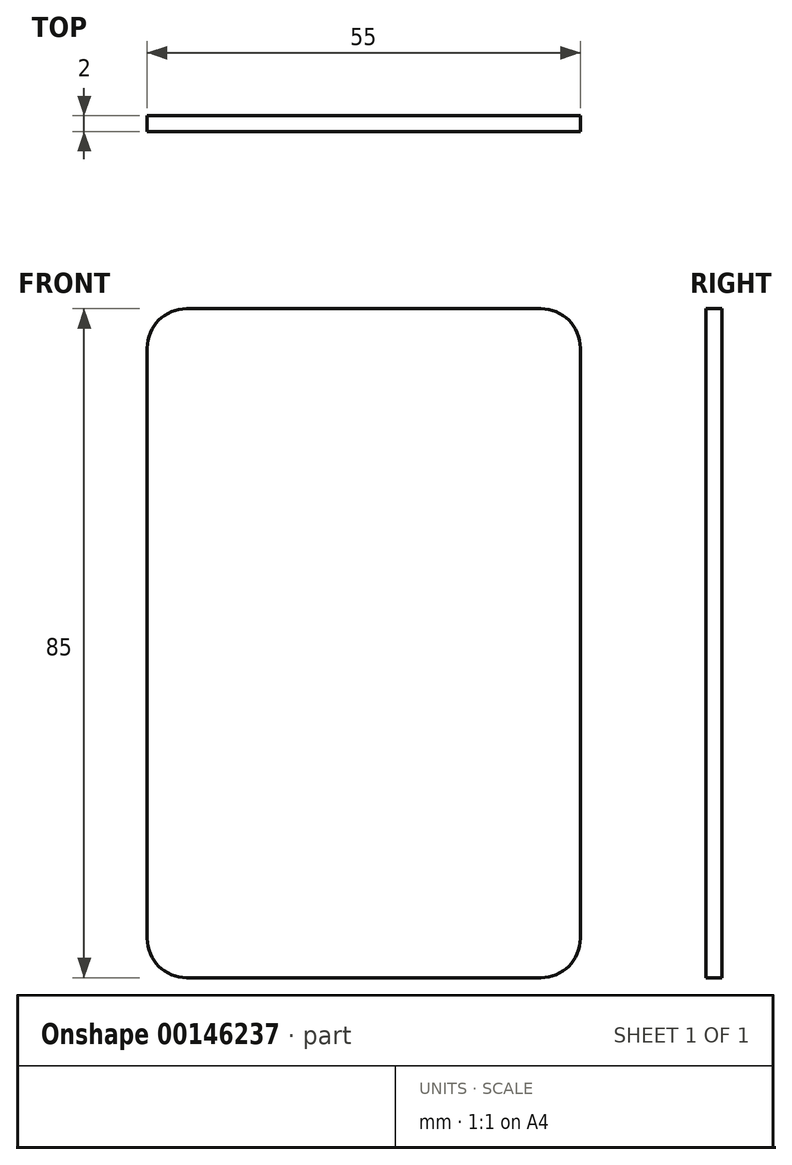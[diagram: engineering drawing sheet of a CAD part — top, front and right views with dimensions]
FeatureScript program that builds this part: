
annotation { "Feature Type Name" : "Feature", "Feature Type Description" : "" }
export const myFeature = defineFeature(function(context is Context, id is Id, definition is map)
    precondition{}
    {
        {
            var Q0;
            Q0=qCreatedBy(makeId("Front.planeOp"),FACE);
            var sketch = newSketch(context, id + "F0", { "sketchPlane" : qUnion([Q0])});
            skLineSegment(sketch, "E0.bottom", {"start": v(-55.3, 47.47) * mm, "end": v(-10.3, 47.47) * mm});
            skLineSegment(sketch, "E0.top", {"start": v(-55.3, -37.53) * mm, "end": v(-10.3, -37.53) * mm});
            skLineSegment(sketch, "E0.left", {"start": v(-60.3, 42.47) * mm, "end": v(-60.3, -32.53) * mm});
            skLineSegment(sketch, "E0.right", {"start": v(-5.3, 42.47) * mm, "end": v(-5.3, -32.53) * mm});
            skPoint(sketch, "E1.visualSharp", {"position": v(-5.3, 47.47) * mm});
            skArc(sketch, "E1.filletArc", {"start": v(-5.3, 42.47) * mm, "mid": v(-6.77, 46) * mm, "end": v(-10.3, 47.47) * mm});
            skPoint(sketch, "E2.visualSharp", {"position": v(-60.3, 47.47) * mm});
            skArc(sketch, "E2.filletArc", {"start": v(-55.3, 47.47) * mm, "mid": v(-58.84, 46) * mm, "end": v(-60.3, 42.47) * mm});
            skPoint(sketch, "E3.visualSharp", {"position": v(-60.3, -37.53) * mm});
            skArc(sketch, "E3.filletArc", {"start": v(-60.3, -32.53) * mm, "mid": v(-58.84, -36.07) * mm, "end": v(-55.3, -37.53) * mm});
            skPoint(sketch, "E4.visualSharp", {"position": v(-5.3, -37.53) * mm});
            skArc(sketch, "E4.filletArc", {"start": v(-10.3, -37.53) * mm, "mid": v(-6.77, -36.07) * mm, "end": v(-5.3, -32.53) * mm});
            skSolve(sketch);
        }
        {
            var Q0;
            Q0=makeQuery(id+"F0.imprint","IMPRINT",FACE,{"disambiguationData":[TD([[makeQuery(id+"F0.imprint","IMPRINT",EDGE,{"derivedFrom":sQuery(id+"F0.wireOp",EDGE,"E0.bottom")}),-1.0]])]});
            extrude(context, id + "F1", {"entities" : qUnion([Q0]), "depth" : 2 * mm});
        }
    });
